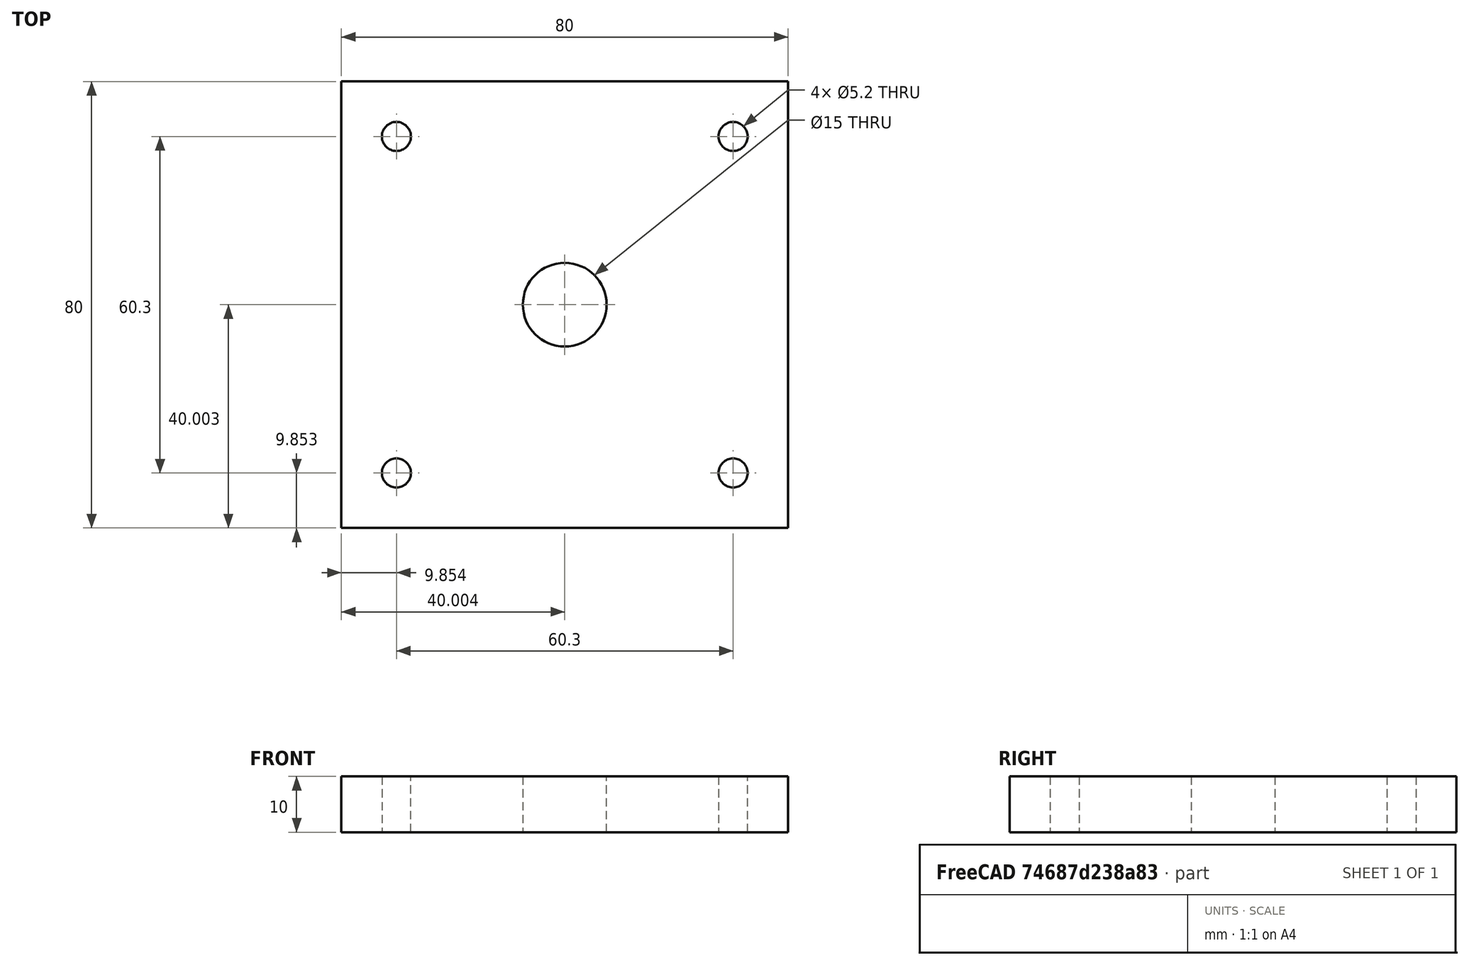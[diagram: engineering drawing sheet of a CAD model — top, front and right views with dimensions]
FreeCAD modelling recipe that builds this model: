
FCSTD DOCUMENT
Label: Motor_plate_FreeCAD
objects: Sketcher::SketchObject×1, PartDesign::Pad×1
note: 3 computed .brp shape members not serialized (recipe doc carries the construction recipe); baked Part::Feature solids carry a one-line shape summary decoded from their .brp

FEATURE [Sketcher::SketchObject] Sketch
  sketch-geometry (9):
    g0: LineSegment StartX=-85.2163 StartY=39.5633 StartZ=0 EndX=-5.21626 EndY=39.5633 EndZ=0
    g1: LineSegment StartX=-5.21626 StartY=39.5633 StartZ=0 EndX=-5.21626 EndY=-40.4367 EndZ=0
    g2: LineSegment StartX=-5.21626 StartY=-40.4367 StartZ=0 EndX=-85.2163 EndY=-40.4367 EndZ=0
    g3: LineSegment StartX=-85.2163 StartY=-40.4367 StartZ=0 EndX=-85.2163 EndY=39.5633 EndZ=0
    g4: Circle CenterX=-75.3663 CenterY=29.7133 CenterZ=0 NormalX=0 NormalY=0 NormalZ=1 Radius=2.6
    g5: Circle CenterX=-15.0663 CenterY=29.7133 CenterZ=0 NormalX=0 NormalY=0 NormalZ=1 Radius=2.6
    g6: Circle CenterX=-15.0663 CenterY=-30.5867 CenterZ=0 NormalX=0 NormalY=0 NormalZ=1 Radius=2.6
    g7: Circle CenterX=-75.3663 CenterY=-30.5867 CenterZ=0 NormalX=0 NormalY=0 NormalZ=1 Radius=2.6
    g8: Circle CenterX=-45.2163 CenterY=-0.436697 CenterZ=0 NormalX=0 NormalY=0 NormalZ=1 Radius=7.5
  constraints (25):
    c: Coincident(g0,g1)
    c: Coincident(g1,g2)
    c: Coincident(g2,g3)
    c: Coincident(g3,g0)
    c: Horizontal(g0)
    c: Horizontal(g2)
    c: Vertical(g1)
    c: Vertical(g3)
    c: DistanceX(g0) = 80
    c: DistanceY(g3) = 80
    c: Radius(g4) = 2.6
    c: Distance(g4,g3) = 9.85
    c: Distance(g4,g0) = 9.85
    c: Distance(g5,g1) = 9.85
    c: Distance(g5,g0) = 9.85
    c: Distance(g6,g1) = 9.85
    c: Distance(g6,g2) = 9.85
    c: Distance(g7,g2) = 9.85
    c: Distance(g7,g3) = 9.85
    c: Distance(g8,g0) = 40
    c: Distance(g8,g3) = 40
    c: Radius(g5) = 2.6
    c: Radius(g6) = 2.6
    c: Radius(g7) = 2.6
    c: Radius(g8) = 7.5
FEATURE [PartDesign::Pad] Pad
  Length = 10
  Length2 = 100
  Sketch = -> Sketch
  Type = 0
